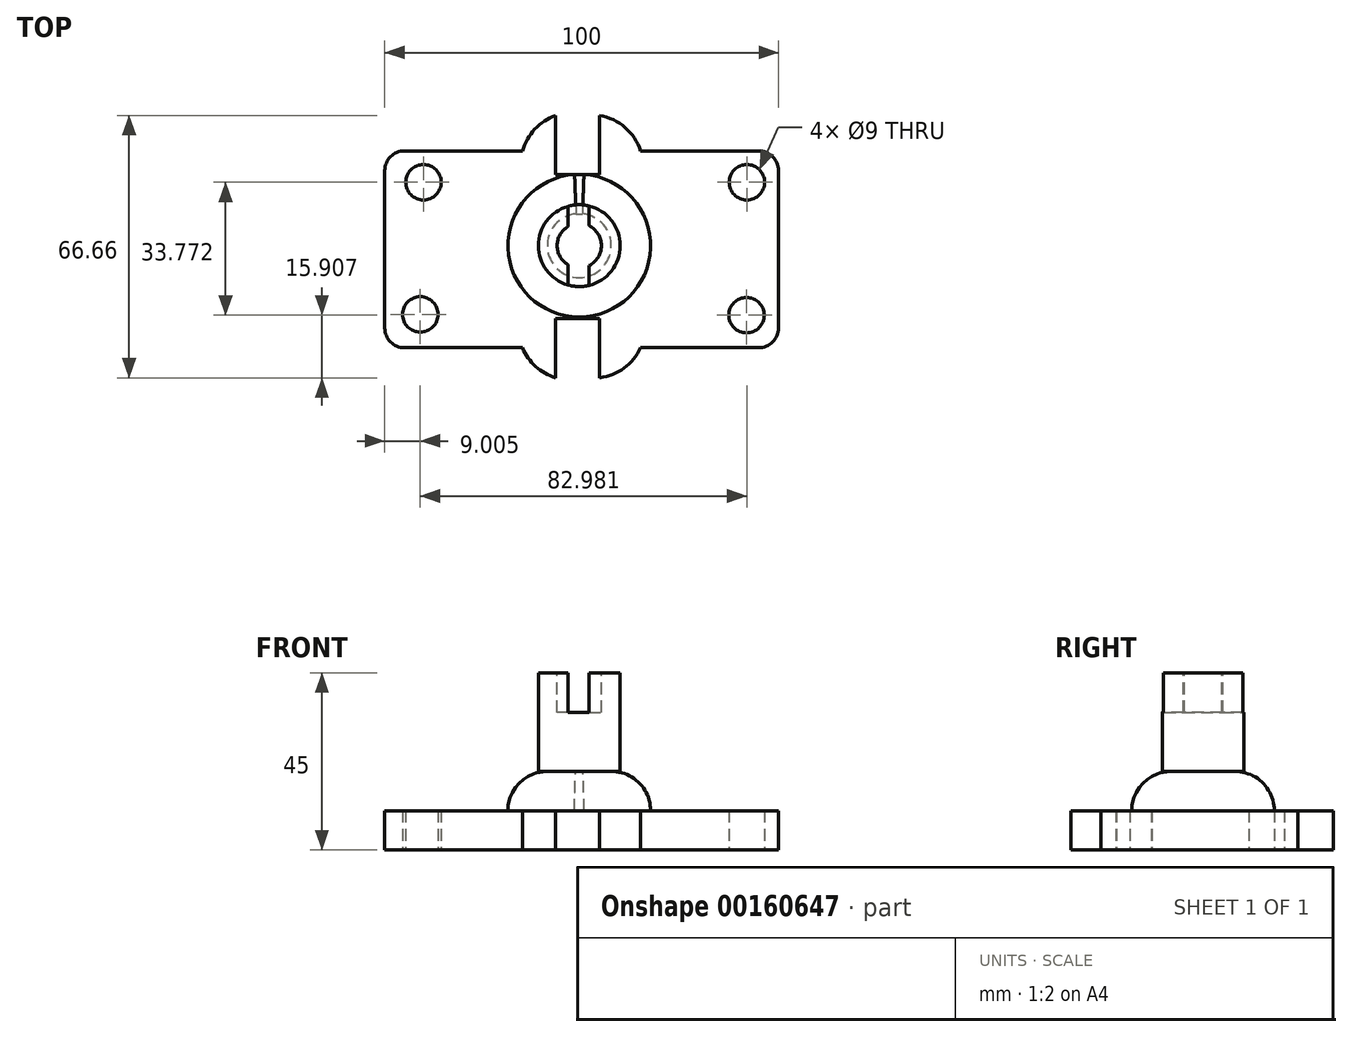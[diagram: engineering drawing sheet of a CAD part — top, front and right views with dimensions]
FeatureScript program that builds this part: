
annotation { "Feature Type Name" : "Feature", "Feature Type Description" : "" }
export const myFeature = defineFeature(function(context is Context, id is Id, definition is map)
    precondition{}
    {
        {
            var Q0;
            Q0=qCreatedBy(makeId("Top.planeOp"),FACE);
            var sketch = newSketch(context, id + "F0", { "sketchPlane" : qUnion([Q0])});
            skLineSegment(sketch, "E0.bottom", {"start": v(40.4, 31.3) * mm, "end": v(10.4, 31.3) * mm});
            skLineSegment(sketch, "E0.top", {"start": v(40.4, -18.7) * mm, "end": v(10.4, -18.7) * mm});
            skLineSegment(sketch, "E0.left", {"start": v(45.4, 26.3) * mm, "end": v(45.4, -13.7) * mm});
            skLineSegment(sketch, "E0.right", {"start": v(-54.6, 26.3) * mm, "end": v(-54.6, -13.7) * mm});
            skPoint(sketch, "E1.visualSharp", {"position": v(-54.6, 31.3) * mm});
            skArc(sketch, "E1.filletArc", {"start": v(-49.6, 31.3) * mm, "mid": v(-53.13, 29.84) * mm, "end": v(-54.6, 26.3) * mm});
            skPoint(sketch, "E2.visualSharp", {"position": v(45.4, 31.3) * mm});
            skArc(sketch, "E2.filletArc", {"start": v(45.4, 26.3) * mm, "mid": v(43.94, 29.84) * mm, "end": v(40.4, 31.3) * mm});
            skPoint(sketch, "E3.visualSharp", {"position": v(45.4, -18.7) * mm});
            skArc(sketch, "E3.filletArc", {"start": v(40.4, -18.7) * mm, "mid": v(43.94, -17.23) * mm, "end": v(45.4, -13.7) * mm});
            skPoint(sketch, "E4.visualSharp", {"position": v(-54.6, -18.7) * mm});
            skArc(sketch, "E4.filletArc", {"start": v(-54.6, -13.7) * mm, "mid": v(-53.13, -17.23) * mm, "end": v(-49.6, -18.7) * mm});
            skCircle(sketch, "E5", {"center": v(37.4, 23.34) * mm, "radius": 4.5 * mm});
            skCircle(sketch, "E6", {"center": v(37.31, -10.43) * mm, "radius": 4.5 * mm});
            skCircle(sketch, "E7", {"center": v(-45.58, -10.24) * mm, "radius": 4.5 * mm});
            skCircle(sketch, "E8", {"center": v(-44.77, 23.34) * mm, "radius": 4.5 * mm});
            skLineSegment(sketch, "E9", {"start": v(-19.6, -18.7) * mm, "end": v(-49.6, -18.7) * mm});
            skArc(sketch, "E10", {"start": v(-19.6, -18.7) * mm, "mid": v(-16.24, -23.45) * mm, "end": v(-11.2, -26.34) * mm});
            skArc(sketch, "E11", {"start": v(10.4, -18.7) * mm, "mid": v(6.18, -23.85) * mm, "end": v(0, -26.34) * mm});
            skLineSegment(sketch, "E12", {"start": v(-11.2, -26.34) * mm, "end": v(0, -26.34) * mm});
            skLineSegment(sketch, "E13", {"start": v(-11.2, -26.34) * mm, "end": v(-11.2, -13.53) * mm});
            skLineSegment(sketch, "E14", {"start": v(-11.2, -13.53) * mm, "end": v(0, -13.53) * mm});
            skLineSegment(sketch, "E15", {"start": v(0, -13.53) * mm, "end": v(0, -26.34) * mm});
            skLineSegment(sketch, "E16", {"start": v(-19.6, 31.3) * mm, "end": v(-49.6, 31.3) * mm});
            skArc(sketch, "E17", {"start": v(-19.6, 31.3) * mm, "mid": v(-16.49, 36.83) * mm, "end": v(-11.2, 40.32) * mm});
            skArc(sketch, "E18", {"start": v(10.4, 31.3) * mm, "mid": v(6.45, 37.25) * mm, "end": v(0, 40.32) * mm});
            skLineSegment(sketch, "E19", {"start": v(-11.2, 40.32) * mm, "end": v(0, 40.32) * mm});
            skLineSegment(sketch, "E20", {"start": v(0, 40.32) * mm, "end": v(0, 27.5) * mm});
            skLineSegment(sketch, "E21", {"start": v(0, 27.5) * mm, "end": v(-11.19, 27.5) * mm});
            skLineSegment(sketch, "E22", {"start": v(-11.19, 27.5) * mm, "end": v(-11.2, 40.32) * mm});
            skSolve(sketch);
        }
        {
            var Q0;
            Q0 = qSketchRegion(id + "F0", true);
            extrude(context, id + "F1", {"entities" : qUnion([Q0]), "depth" : 10 * mm});
        }
        {
            var Q0;
            Q0=makeQuery(id+"F1.opExtrude","SWEPT_FACE",FACE,{"disambiguationData":[OSD([sQuery(id+"F0.wireOp",EDGE,"E12")])]});
            extrude(context, id + "F2", {"entities" : qUnion([Q0]), "operationType" : NewBodyOperationType.REMOVE, "oppositeDirection" : true, "depth" : 15 * mm});
        }
        {
            var Q0;
            Q0=makeQuery(id+"F1.opExtrude","SWEPT_FACE",FACE,{"disambiguationData":[OSD([sQuery(id+"F0.wireOp",EDGE,"E19")])]});
            extrude(context, id + "F3", {"entities" : qUnion([Q0]), "operationType" : NewBodyOperationType.REMOVE, "oppositeDirection" : true, "depth" : 15 * mm});
        }
        {
            var Q0;
            Q0=makeQuery(id+"F1.opExtrude","CAP_FACE",FACE,{"disambiguationData":[OSD([sQuery(id+"F0.wireOp",EDGE,"E0.bottom"),sQuery(id+"F0.wireOp",EDGE,"E0.top"),sQuery(id+"F0.wireOp",EDGE,"E0.left"),sQuery(id+"F0.wireOp",EDGE,"E0.right"),sQuery(id+"F0.wireOp",EDGE,"E1.filletArc"),sQuery(id+"F0.wireOp",EDGE,"E2.filletArc"),sQuery(id+"F0.wireOp",EDGE,"E3.filletArc"),sQuery(id+"F0.wireOp",EDGE,"E4.filletArc"),sQuery(id+"F0.wireOp",EDGE,"E5"),sQuery(id+"F0.wireOp",EDGE,"E6"),sQuery(id+"F0.wireOp",EDGE,"E7"),sQuery(id+"F0.wireOp",EDGE,"E8"),sQuery(id+"F0.wireOp",EDGE,"E9"),sQuery(id+"F0.wireOp",EDGE,"E10"),sQuery(id+"F0.wireOp",EDGE,"E11"),sQuery(id+"F0.wireOp",EDGE,"E12"),sQuery(id+"F0.wireOp",EDGE,"E16"),sQuery(id+"F0.wireOp",EDGE,"E17"),sQuery(id+"F0.wireOp",EDGE,"E18"),sQuery(id+"F0.wireOp",EDGE,"E19")])],"isStart":false});
            var sketch = newSketch(context, id + "F4", { "sketchPlane" : qUnion([Q0])});
            skCircle(sketch, "E23", {"center": v(-5.19, 7.23) * mm, "radius": 18.12 * mm});
            skLineSegment(sketch, "E24", {"start": v(-5.19, 7.23) * mm, "end": v(-5.19, 25.35) * mm});
            skLineSegment(sketch, "E25", {"start": v(-5.19, 25.35) * mm, "end": v(-5.19, -10.89) * mm});
            skSolve(sketch);
        }
        {
            var Q0;
            {var subQ0=sQuery(id+"F4.wireOp",EDGE,"E25");var subQ4=makeQuery(id+"F4.imprint","IMPRINT",VERTEX,{"derivedFrom":subQ0});Q0=makeQuery(id+"F4.imprint","IMPRINT",FACE,{"disambiguationData":[TD([[makeQuery(id+"F4.imprint","IMPRINT",EDGE,{"disambiguationData":[TD([[subQ4,1.0]])],"derivedFrom":subQ0}),-1.0]])]});}
            var Q1;
            {var subQ0=sQuery(id+"F4.wireOp",EDGE,"E25");var subQ4=makeQuery(id+"F4.imprint","IMPRINT",VERTEX,{"derivedFrom":subQ0});Q1=makeQuery(id+"F4.imprint","IMPRINT",FACE,{"disambiguationData":[TD([[makeQuery(id+"F4.imprint","IMPRINT",EDGE,{"disambiguationData":[TD([[subQ4,1.0]])],"derivedFrom":subQ0}),1.0]])]});}
            extrude(context, id + "F5", {"entities" : qUnion([Q0, Q1]), "operationType" : NewBodyOperationType.ADD, "depth" : 10 * mm});
        }
        {
            var Q0;
            Q0=makeQuery(id+"F5.opExtrude","CAP_FACE",FACE,{"disambiguationData":[OSD([sQuery(id+"F0.wireOp",EDGE,"E19"),sQuery(id+"F4.wireOp",EDGE,"E23")])],"isStart":false});
            fillet(context, id + "F6", {"entities" : qUnion([Q0]), "radius" : 10 * mm, "tangentPropagation" : true, "allowEdgeOverflow" : false});
        }
        {
            var Q0;
            Q0=makeQuery(id+"F5.opExtrude","CAP_FACE",FACE,{"disambiguationData":[OSD([sQuery(id+"F0.wireOp",EDGE,"E19"),sQuery(id+"F4.wireOp",EDGE,"E23")])],"isStart":false});
            var sketch = newSketch(context, id + "F7", { "sketchPlane" : qUnion([Q0])});
            skCircle(sketch, "E26", {"center": v(-5.19, 7.23) * mm, "radius": 10.4 * mm});
            skSolve(sketch);
        }
        {
            var Q0;
            Q0 = qSketchRegion(id + "F7", true);
            extrude(context, id + "F8", {"entities" : qUnion([Q0]), "operationType" : NewBodyOperationType.ADD, "depth" : 25 * mm});
        }
        {
            var Q0;
            Q0=makeQuery(id+"F8.opExtrude","CAP_FACE",FACE,{"disambiguationData":[OSD([sQuery(id+"F7.wireOp",EDGE,"E26")])],"isStart":false});
            var sketch = newSketch(context, id + "F9", { "sketchPlane" : qUnion([Q0])});
            skLineSegment(sketch, "E27", {"start": v(-2.73, 17.33) * mm, "end": v(-2.73, -2.87) * mm});
            skLineSegment(sketch, "E28", {"start": v(-8.1, -2.74) * mm, "end": v(-8.1, 17.2) * mm});
            skSolve(sketch);
        }
        {
            var Q0;
            Q0 = qSketchRegion(id + "F9", true);
            var Q1;
            {var subQ0=sQuery(id+"F9.wireOp",EDGE,"E27");Q1=makeQuery(id+"F9.imprint","IMPRINT",FACE,{"disambiguationData":[TD([[makeQuery(id+"F9.imprint","IMPRINT",EDGE,{"derivedFrom":subQ0}),-1.0]])]});}
            extrude(context, id + "F10", {"entities" : qUnion([Q0, Q1]), "operationType" : NewBodyOperationType.REMOVE, "oppositeDirection" : true, "depth" : 10 * mm});
        }
        {
            var Q0;
            {var subQ0=sQuery(id+"F7.wireOp",EDGE,"E26");Q0=makeQuery(id+"F10.boolean.opBoolean","SPLIT",FACE,{"disambiguationData":[TD([makeQuery(id+"F10.opExtrude","SWEPT_FACE",FACE,{"disambiguationData":[OSD([sQuery(id+"F9.wireOp",EDGE,"E28")])]})])],"derivedFrom":makeQuery(id+"F8.opExtrude","CAP_FACE",FACE,{"disambiguationData":[OSD([subQ0])],"isStart":false})});}
            var sketch = newSketch(context, id + "F11", { "sketchPlane" : qUnion([Q0])});
            skCircle(sketch, "E29", {"center": v(-5.19, 7.23) * mm, "radius": 5.63 * mm});
            skSolve(sketch);
        }
        {
            var Q0;
            Q0 = qSketchRegion(id + "F11", true);
            extrude(context, id + "F12", {"entities" : qUnion([Q0]), "operationType" : NewBodyOperationType.REMOVE, "oppositeDirection" : true, "depth" : 10 * mm});
        }
    });
